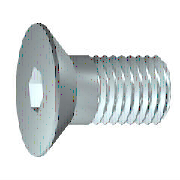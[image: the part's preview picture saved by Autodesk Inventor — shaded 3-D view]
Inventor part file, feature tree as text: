
AUTODESK INVENTOR PART (.ipt)
format: ipt  version: 2020 (Build 240168000, 168)  size: 186,880 bytes
history: native  units: mm (DEFAULTED — no unit token found)
features: other x4, sketch x3, fillet x1, chamfer x1
ambient origin geometry x8: Origin, YZ Plane, XZ Plane, XY Plane, X Axis, Y Axis, Z Axis, Center Point
bodies: Solid1 (feature_tree)
feature tree (9):
  sketch  "Sketch1"  dims[d2=3.0mm]
  other  "WorkPoint1"
  sketch  "Sketch2"  dims[d3=3.0mm]
  fillet  "Fillet1"  [1 undecoded]
  chamfer  "Chamfer1"  Distance=1.5mm
  other  "MSC_A1"
  other  "MSC_PF1"
  other  "MSC_PT1"
  sketch  "Sketch3"  dims[d4=1.5mm d5=1.5mm d6=8.0mm d7=20.0mm d8=360.0deg d9=0.0mm d10=2.0mm d11=2.0mm d12=120.0deg d13=120.0deg d14=120.0deg d15=120.0deg d16=1.2mm d17=0.0mm d18=0.1mm d19=0.25mm d20=45.0deg d22=0.0mm d23=0.0mm d35=0.0mm d37=0.0mm d38=0.0mm d39=0.25mm d40=0.0mm d41=0.0mm d42=0.0mm d43=45.0deg]
note: 1 required parameter value undecoded (feature->parameter linkage not recoverable at this tier; creation-order binding heuristic only, values carry confidence <= 0.55)
